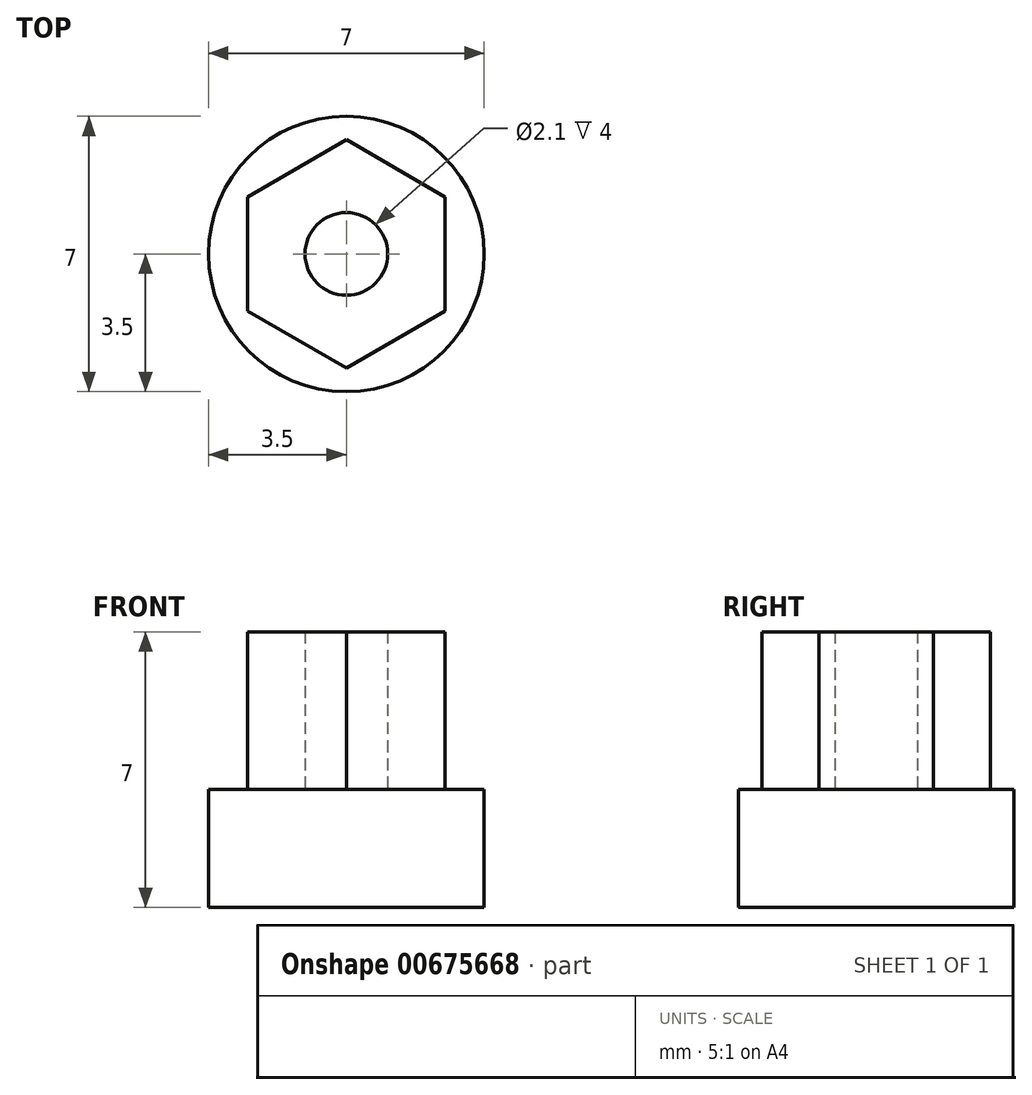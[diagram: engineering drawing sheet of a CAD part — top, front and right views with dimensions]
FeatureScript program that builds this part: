
annotation { "Feature Type Name" : "Feature", "Feature Type Description" : "" }
export const myFeature = defineFeature(function(context is Context, id is Id, definition is map)
    precondition{}
    {
        {
            var Q0;
            Q0=qCreatedBy(makeId("Top.planeOp"),FACE);
            var sketch = newSketch(context, id + "F0", { "sketchPlane" : qUnion([Q0])});
            skCircle(sketch, "E0", {"center": v(0, 0) * mm, "radius": 2.9 * mm});
            skLineSegment(sketch, "E1", {"start": v(0, 2.9) * mm, "end": v(0, -2.9) * mm});
            skLineSegment(sketch, "E2", {"start": v(0, -2.9) * mm, "end": v(2.51, -1.45) * mm});
            skLineSegment(sketch, "E3", {"start": v(0, 2.9) * mm, "end": v(2.51, 1.45) * mm});
            skLineSegment(sketch, "E4", {"start": v(2.51, 1.45) * mm, "end": v(2.51, -1.45) * mm});
            skLineSegment(sketch, "E5", {"start": v(0, 2.9) * mm, "end": v(-2.51, 1.45) * mm});
            skLineSegment(sketch, "E6", {"start": v(-2.51, 1.45) * mm, "end": v(-2.51, -1.45) * mm});
            skLineSegment(sketch, "E7", {"start": v(-2.51, -1.45) * mm, "end": v(0, -2.9) * mm});
            skCircle(sketch, "E8", {"center": v(0, 0) * mm, "radius": 1.05 * mm});
            skSolve(sketch);
        }
        {
            var Q0;
            {var subQ1=sQuery(id+"F0.wireOp",EDGE,"E2");Q0=makeQuery(id+"F0.imprint","IMPRINT",FACE,{"disambiguationData":[TD([[makeQuery(id+"F0.imprint","IMPRINT",EDGE,{"derivedFrom":subQ1}),1.0]])]});}
            var Q1;
            {var subQ0=sQuery(id+"F0.wireOp",EDGE,"E5");Q1=makeQuery(id+"F0.imprint","IMPRINT",FACE,{"disambiguationData":[TD([[makeQuery(id+"F0.imprint","IMPRINT",EDGE,{"derivedFrom":subQ0}),1.0]])]});}
            extrude(context, id + "F1", {"entities" : qUnion([Q0, Q1]), "depth" : 4 * mm, "offsetDistance" : 25 * mm});
        }
        {
            var Q0;
            Q0=makeQuery(id+"F1.opExtrude","CAP_FACE",FACE,{"disambiguationData":[OSD([sQuery(id+"F0.wireOp",EDGE,"E2"),sQuery(id+"F0.wireOp",EDGE,"E3"),sQuery(id+"F0.wireOp",EDGE,"E4"),sQuery(id+"F0.wireOp",EDGE,"E5"),sQuery(id+"F0.wireOp",EDGE,"E6"),sQuery(id+"F0.wireOp",EDGE,"E7"),sQuery(id+"F0.wireOp",EDGE,"E8")])],"isStart":true});
            var sketch = newSketch(context, id + "F2", { "sketchPlane" : qUnion([Q0])});
            skCircle(sketch, "E9", {"center": v(0, 0) * mm, "radius": 3.5 * mm});
            skSolve(sketch);
        }
        {
            var Q0;
            Q0=makeQuery(id+"F2.imprint","IMPRINT",FACE,{"disambiguationData":[TD([[makeQuery(id+"F2.imprint","IMPRINT",EDGE,{"derivedFrom":sQuery(id+"F2.wireOp",EDGE,"E9")}),1.0]])]});
            var Q1;
            Q1=makeQuery(id+"F2.imprint","IMPRINT",FACE,{"disambiguationData":[TD([[makeQuery(id+"F2.imprint","IMPRINT",EDGE,{"derivedFrom":makeQuery(id+"F1.opExtrude","CAP_EDGE",EDGE,{"disambiguationData":[OSD([sQuery(id+"F0.wireOp",EDGE,"E2")])],"isStart":true})}),-1.0]])]});
            var Q2;
            Q2=makeQuery(id+"F2.imprint","IMPRINT",FACE,{"disambiguationData":[TD([[makeQuery(id+"F2.imprint","IMPRINT",EDGE,{"derivedFrom":makeQuery(id+"F1.opExtrude","CAP_EDGE",EDGE,{"disambiguationData":[OSD([sQuery(id+"F0.wireOp",EDGE,"E8")])],"isStart":true})}),-1.0]])]});
            extrude(context, id + "F3", {"entities" : qUnion([Q0, Q1, Q2]), "operationType" : NewBodyOperationType.ADD, "depth" : 3 * mm, "offsetDistance" : 25 * mm});
        }
    });
